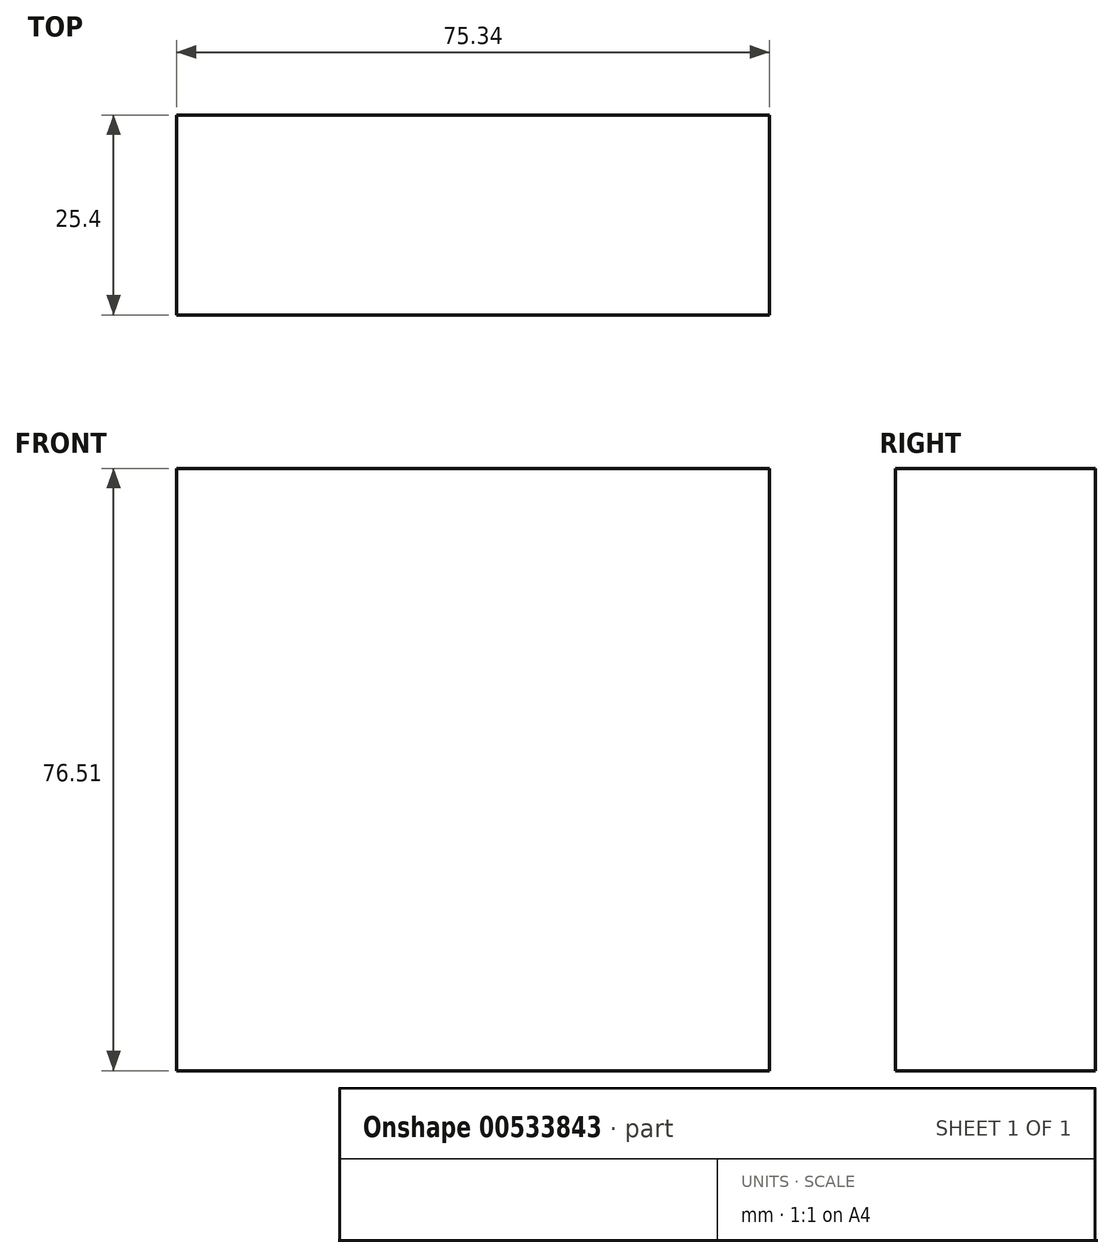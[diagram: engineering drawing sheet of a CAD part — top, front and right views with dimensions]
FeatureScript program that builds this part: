
annotation { "Feature Type Name" : "Feature", "Feature Type Description" : "" }
export const myFeature = defineFeature(function(context is Context, id is Id, definition is map)
    precondition{}
    {
        {
            var Q0;
            Q0=qCreatedBy(makeId("Front.planeOp"),FACE);
            var sketch = newSketch(context, id + "F0", { "sketchPlane" : qUnion([Q0])});
            skLineSegment(sketch, "E0.bottom", {"start": v(-36.2, 37.67) * mm, "end": v(39.13, 37.67) * mm});
            skLineSegment(sketch, "E0.top", {"start": v(-36.2, -38.84) * mm, "end": v(39.13, -38.84) * mm});
            skLineSegment(sketch, "E0.left", {"start": v(-36.2, 37.67) * mm, "end": v(-36.2, -38.84) * mm});
            skLineSegment(sketch, "E0.right", {"start": v(39.13, 37.67) * mm, "end": v(39.13, -38.84) * mm});
            skSolve(sketch);
        }
        {
            var Q0;
            Q0=makeQuery(id+"F0.imprint","IMPRINT",FACE,{"disambiguationData":[TD([[makeQuery(id+"F0.imprint","IMPRINT",EDGE,{"derivedFrom":sQuery(id+"F0.wireOp",EDGE,"E0.bottom")}),-1.0]])]});
            extrude(context, id + "F1", {"entities" : qUnion([Q0]), "depth" : 25.4 * mm, "offsetDistance" : 25.4 * mm});
        }
    });
